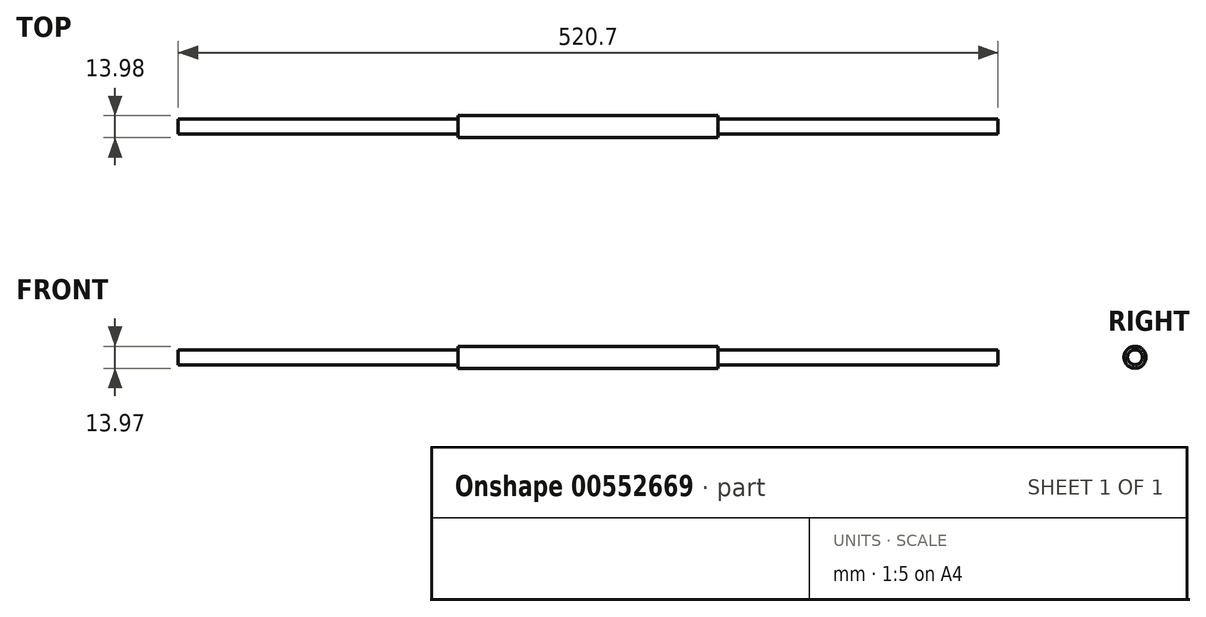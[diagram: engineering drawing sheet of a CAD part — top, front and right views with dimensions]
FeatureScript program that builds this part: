
annotation { "Feature Type Name" : "Feature", "Feature Type Description" : "" }
export const myFeature = defineFeature(function(context is Context, id is Id, definition is map)
    precondition{}
    {
        {
            var Q0;
            Q0=qCreatedBy(makeId("Front.planeOp"),FACE);
            var sketch = newSketch(context, id + "F0", { "sketchPlane" : qUnion([Q0])});
            skLineSegment(sketch, "E0", {"start": v(-252.52, 14.31) * mm, "end": v(268.18, 14.31) * mm});
            skLineSegment(sketch, "E1", {"start": v(7.83, 16.54) * mm, "end": v(-74.72, 16.54) * mm});
            skLineSegment(sketch, "E2", {"start": v(-74.72, 16.54) * mm, "end": v(-74.72, 14.31) * mm});
            skLineSegment(sketch, "E3.MirrorCS", {"start": v(7.83, 16.54) * mm, "end": v(90.38, 16.54) * mm});
            skLineSegment(sketch, "E4.MirrorCS", {"start": v(90.38, 16.54) * mm, "end": v(90.38, 14.31) * mm});
            skPoint(sketch, "E5.start.orphan", {"position": v(7.83, 14.31) * mm});
            skLineSegment(sketch, "E6.0", {"start": v(-252.52, 9.55) * mm, "end": v(268.18, 9.55) * mm});
            skLineSegment(sketch, "E7", {"start": v(-252.52, 9.55) * mm, "end": v(-252.52, 14.31) * mm});
            skLineSegment(sketch, "E8", {"start": v(268.18, 9.55) * mm, "end": v(268.18, 14.31) * mm});
            skSolve(sketch);
        }
        {
            var Q0;
            Q0 = qSketchRegion(id + "F0", true);
            var Q1;
            Q1=sQuery(id+"F0.wireOp",EDGE,"E6.0");
            revolve(context, id + "F1", {"entities" : qUnion([Q0]), "axis" : qUnion([Q1]), "revolveType" : RevolveType.FULL});
        }
    });
